# Revit family: IS_ConnectAir_E0155_BIM_DE
name_source: partatom
category: Plumbing Fixtures
revit_build: Autodesk Revit MEP 2014 (Build: 20130308_1515(x64)
units: mm (PartAtom-declared; Revit-internal decimal feet)

## types (2) — shared parameters
Accessories = www.idealstandard.de\ersatzteile
AreaUnits = millimeters
Assembly Code = C1030200
AssetType = Fixed
Brand = Ideal Standard
CodePerformance = DIN EN 997 CL1-6AC/5A, DIN EN 33
ConnectionType = Plumbing
DurationUnit = year
ExpectedLife = 25
Features = Connect Air wall mounted bowl, wash-down, rimless
GrossWeight = 0
IfcExportAs = IfcSanitaryTerminalType
IfcExportType = TOILETPAN
InstallationInstructions = www.idealstandard.de\produkte
LinearUnits = millimeters
ManufacturerURL = www.idealstandard.com
NBSDescription = WC pans
NBSReference = 45-30-70/384
NominalHeight = 352 mm
NominalLength = 539 mm
NominalWidth = 360 mm
PanMaterial = Vitreous china
PanMounting = BackToWall
ProductInformation = www.idealstandard.de/produkte
Shape = Sculptured
Size = 360x540x340mm
Space = Internal
ToiletPanType = WashDown
ToiletType = Other
URL = www.idealstandard.com
Uniclass2015Code = Pr_40_20_93_94
Uniclass2015Title = WC pans
Uniclass2015Version = Products v1.1
Version = 1
VolumeUnits = Litres
WarrantyDescription = Manufacturers Warranty
WarrantyDurationUnit = year
zero-valued in all types: CWFU, Cost, HWFU, SpilloverLevel, WFU

## per-type parameters (varying)
| type | BIMObjectName | BarCode | Default Elevation | Description | Finish | Model | ModelNumber | ModelReference | Name | NettWeight | PanColor |
| E015501 Connect Air back-to wall bowl, wash down, rimless | ISI_IdealStandard_WcPans_ConnectAir_E015501 | 5017830514282 | 400 mm  [stored 1.31234 ft] | E015501 Connect Air wall mounted bowl, wash-down, rimless | white | E015501 | E015501 | Connect Air back-to wall bowl, wash down, rimless | WcPans_ConnectAir_E015501_IdealStandard | 22,2 kg | White |
| E0155MA Connect Air back-to wall bowl, wash down, rimless, with Ideal Plus | ISI_IdealStandard_WcPans_ConnectAir_E0155MA | 5017830518297 | 0 mm  [stored 0 ft] | E0155MA Connect Air wall mounted bowl, wash-down, rimless | white with ideal plus | E0155MA | E0155MA | Connect Air back-to wall bowl, wash down, rimless, with Ideal Plus | WcPans_ConnectAir_E0155MA_IdealStandard | 23,6 kg | White with Ideal Plus |

note: [stored X ft] marks values corroborated as IEEE doubles in the binary element streams (Revit-internal decimal feet)

## geometry (parser evidence)
native form markers: Sweep x3
no freeform markers — native parametric forms only
